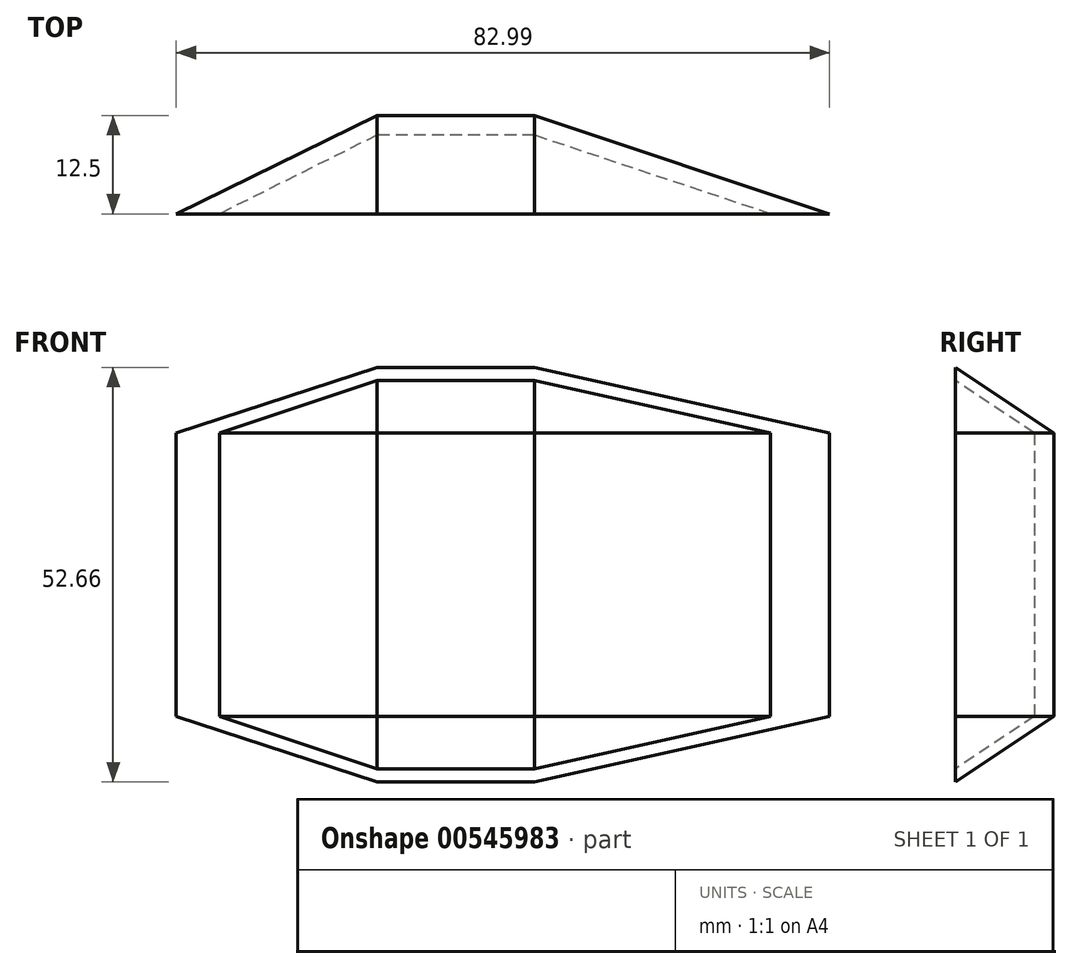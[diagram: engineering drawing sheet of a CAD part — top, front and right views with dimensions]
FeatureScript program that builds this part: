
annotation { "Feature Type Name" : "Feature", "Feature Type Description" : "" }
export const myFeature = defineFeature(function(context is Context, id is Id, definition is map)
    precondition{}
    {
        {
            var Q0;
            Q0=qCreatedBy(makeId("Top.planeOp"),FACE);
            var sketch = newSketch(context, id + "F0", { "sketchPlane" : qUnion([Q0])});
            skLineSegment(sketch, "E0", {"start": v(-20, 0) * mm, "end": v(20, 0) * mm});
            skLineSegment(sketch, "E1", {"start": v(20, 0) * mm, "end": v(50, 0) * mm});
            skLineSegment(sketch, "E2", {"start": v(50, 0) * mm, "end": v(20, 10) * mm});
            skLineSegment(sketch, "E3", {"start": v(20, 10) * mm, "end": v(20, 0) * mm});
            skLineSegment(sketch, "E4", {"start": v(20, 10) * mm, "end": v(0, 10) * mm});
            skLineSegment(sketch, "E5", {"start": v(0, 10) * mm, "end": v(-20, 0) * mm});
            skLineSegment(sketch, "E6", {"start": v(0, 0) * mm, "end": v(0, -2.5) * mm});
            skLineSegment(sketch, "E7", {"start": v(0, -2.5) * mm, "end": v(-30.6, -2.5) * mm});
            skLineSegment(sketch, "E8", {"start": v(-30.6, -2.5) * mm, "end": v(0, 12.5) * mm});
            skLineSegment(sketch, "E9", {"start": v(-10, 5) * mm, "end": v(-11.04, 7.09) * mm});
            skLineSegment(sketch, "E10", {"start": v(20, 10) * mm, "end": v(20, 12.5) * mm});
            skLineSegment(sketch, "E11", {"start": v(0, 12.5) * mm, "end": v(20, 12.5) * mm});
            skLineSegment(sketch, "E12", {"start": v(0, 12.5) * mm, "end": v(0, 10) * mm});
            skLineSegment(sketch, "E13", {"start": v(0, -2.5) * mm, "end": v(65, -2.5) * mm});
            skLineSegment(sketch, "E14", {"start": v(65, -2.5) * mm, "end": v(20, 12.5) * mm});
            skSolve(sketch);
        }
        {
            var Q0;
            {var subQ2=sQuery(id+"F0.wireOp",EDGE,"E9");Q0=makeQuery(id+"F0.imprint","IMPRINT",FACE,{"disambiguationData":[TD([[makeQuery(id+"F0.imprint","IMPRINT",EDGE,{"derivedFrom":subQ2}),-1.0]])]});}
            var Q1;
            {var subQ1=sQuery(id+"F0.wireOp",EDGE,"E6");Q1=makeQuery(id+"F0.imprint","IMPRINT",FACE,{"disambiguationData":[TD([[makeQuery(id+"F0.imprint","IMPRINT",EDGE,{"derivedFrom":subQ1}),-1.0]])]});}
            var Q2;
            {var subQ1=sQuery(id+"F0.wireOp",EDGE,"E1");Q2=makeQuery(id+"F0.imprint","IMPRINT",FACE,{"disambiguationData":[TD([[makeQuery(id+"F0.imprint","IMPRINT",EDGE,{"derivedFrom":subQ1}),-1.0]])]});}
            var Q3;
            Q3=makeQuery(id+"F0.imprint","IMPRINT",FACE,{"disambiguationData":[TD([[makeQuery(id+"F0.imprint","IMPRINT",EDGE,{"derivedFrom":sQuery(id+"F0.wireOp",EDGE,"E4")}),-1.0]])]});
            extrude(context, id + "F1", {"entities" : qUnion([Q0, Q1, Q2, Q3]), "depth" : 36 * mm, "offsetDistance" : 25 * mm});
        }
        {
            var Q0;
            Q0=qCreatedBy(makeId("Right.planeOp"),FACE);
            var sketch = newSketch(context, id + "F2", { "sketchPlane" : qUnion([Q0])});
            skLineSegment(sketch, "E15", {"start": v(-2.71, 36) * mm, "end": v(12.29, 36) * mm});
            skLineSegment(sketch, "E16", {"start": v(12.29, 36) * mm, "end": v(-2.71, 46) * mm});
            skLineSegment(sketch, "E17", {"start": v(-2.71, 46) * mm, "end": v(-2.71, 36) * mm});
            skLineSegment(sketch, "E18", {"start": v(-2.71, 36) * mm, "end": v(-2.71, 0) * mm});
            skPoint(sketch, "E19", {"position": v(-2.71, 18) * mm});
            skLineSegment(sketch, "E20", {"start": v(-2.71, 18) * mm, "end": v(12.7, 18) * mm});
            skLineSegment(sketch, "E21.MirrorCS", {"start": v(12.29, 0) * mm, "end": v(-2.71, -10) * mm});
            skSolve(sketch);
        }
        {
            var Q0;
            Q0=makeQuery(id+"F1.opExtrude","CAP_FACE",FACE,{"disambiguationData":[OSD([sQuery(id+"F0.wireOp",EDGE,"E0"),sQuery(id+"F0.wireOp",EDGE,"E1"),sQuery(id+"F0.wireOp",EDGE,"E2"),sQuery(id+"F0.wireOp",EDGE,"E4"),sQuery(id+"F0.wireOp",EDGE,"E5"),sQuery(id+"F0.wireOp",EDGE,"E7"),sQuery(id+"F0.wireOp",EDGE,"E8"),sQuery(id+"F0.wireOp",EDGE,"E11"),sQuery(id+"F0.wireOp",EDGE,"E13"),sQuery(id+"F0.wireOp",EDGE,"E14")])],"isStart":false});
            var Q1;
            Q1=sQuery(id+"F2.wireOp",EDGE,"E16");
            sweep(context, id + "F3", {"operationType" : NewBodyOperationType.ADD, "profiles" : qUnion([Q0]), "path" : qUnion([Q1])});
        }
        {
            var Q0;
            Q0=makeQuery(id+"F1.opExtrude","CAP_FACE",FACE,{"disambiguationData":[OSD([sQuery(id+"F0.wireOp",EDGE,"E0"),sQuery(id+"F0.wireOp",EDGE,"E1"),sQuery(id+"F0.wireOp",EDGE,"E2"),sQuery(id+"F0.wireOp",EDGE,"E4"),sQuery(id+"F0.wireOp",EDGE,"E5"),sQuery(id+"F0.wireOp",EDGE,"E7"),sQuery(id+"F0.wireOp",EDGE,"E8"),sQuery(id+"F0.wireOp",EDGE,"E11"),sQuery(id+"F0.wireOp",EDGE,"E13"),sQuery(id+"F0.wireOp",EDGE,"E14")])],"isStart":true});
            var Q1;
            Q1=sQuery(id+"F2.wireOp",EDGE,"E21.MirrorCS");
            sweep(context, id + "F4", {"operationType" : NewBodyOperationType.ADD, "profiles" : qUnion([Q0]), "path" : qUnion([Q1])});
        }
        {
            var Q0;
            Q0=qCreatedBy(makeId("Front.planeOp"),FACE);
            var sketch = newSketch(context, id + "F5", { "sketchPlane" : qUnion([Q0])});
            skLineSegment(sketch, "E22.bottom", {"start": v(-36.55, 50.38) * mm, "end": v(71.94, 50.38) * mm});
            skLineSegment(sketch, "E22.top", {"start": v(-36.55, -16.57) * mm, "end": v(71.94, -16.57) * mm});
            skLineSegment(sketch, "E22.left", {"start": v(-36.55, 50.38) * mm, "end": v(-36.55, -16.57) * mm});
            skLineSegment(sketch, "E22.right", {"start": v(71.94, 50.38) * mm, "end": v(71.94, -16.57) * mm});
            skSolve(sketch);
        }
        {
            var Q0;
            Q0=makeQuery(id+"F5.imprint","IMPRINT",FACE,{"disambiguationData":[TD([[makeQuery(id+"F5.imprint","IMPRINT",EDGE,{"derivedFrom":sQuery(id+"F5.wireOp",EDGE,"E22.bottom")}),-1.0]])]});
            extrude(context, id + "F6", {"entities" : qUnion([Q0]), "operationType" : NewBodyOperationType.REMOVE, "depth" : 25 * mm, "offsetDistance" : 25 * mm});
        }
    });
